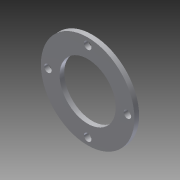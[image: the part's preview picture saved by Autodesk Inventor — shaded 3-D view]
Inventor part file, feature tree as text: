
AUTODESK INVENTOR PART (.ipt)
format: ipt  version: 2013 (Build 170138000, 138)  size: 91,136 bytes
history: native  units: in
note: dims shown in document units (in); Inventor stores cm internally (conversion verified against a paired STEP export)
features: extrude x1, sketch x1
ambient origin geometry x8: Origin, YZ Plane, XZ Plane, XY Plane, X Axis, Y Axis, Z Axis, Center Point
bodies: Solid1 (feature_tree)
feature tree (2):
  extrude  "Extrusion1"  Depth=1.5in
  sketch  "Sketch1"  dims[d0=2.5in d2=1.5in d3=1.063in d4=0.2in d5=1.5748in d7=360.0deg d9=0.125in d10=0.0in]
